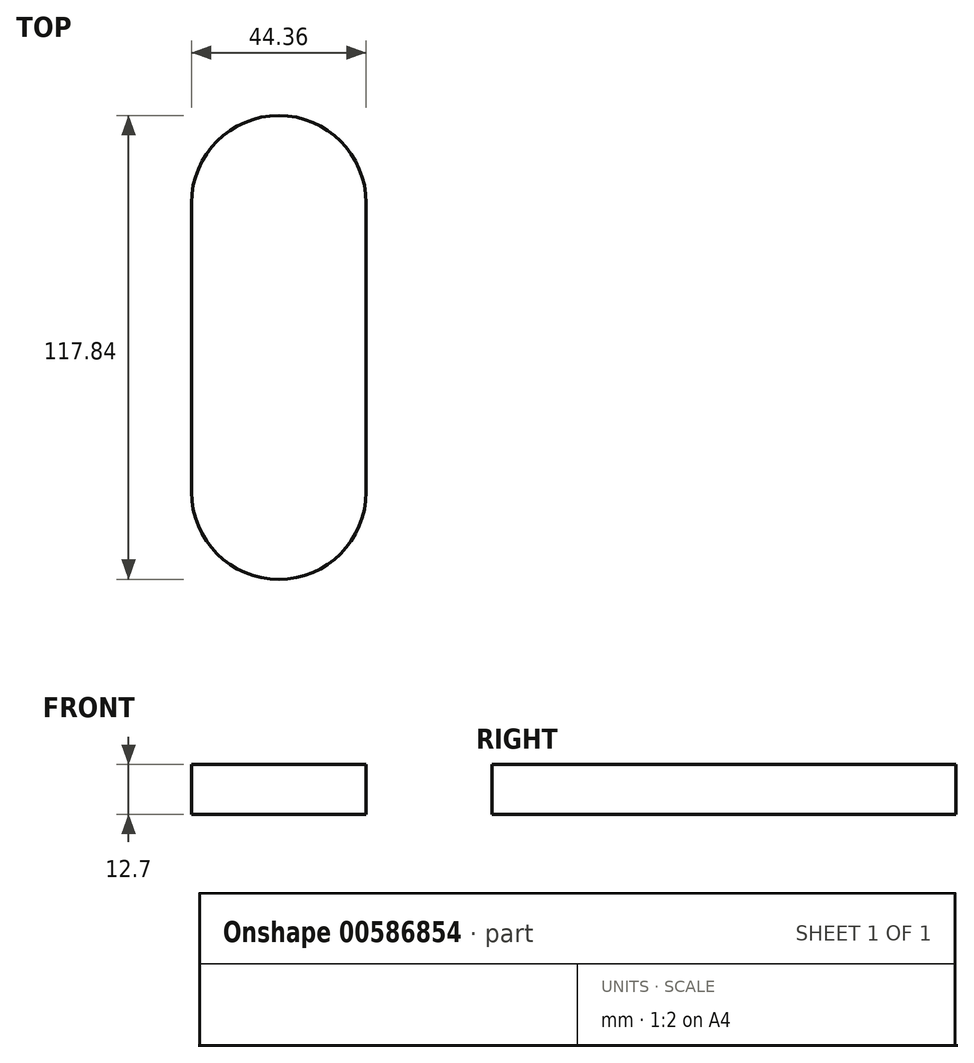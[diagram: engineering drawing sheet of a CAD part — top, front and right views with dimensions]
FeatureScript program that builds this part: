
annotation { "Feature Type Name" : "Feature", "Feature Type Description" : "" }
export const myFeature = defineFeature(function(context is Context, id is Id, definition is map)
    precondition{}
    {
        {
            var Q0;
            Q0=qCreatedBy(makeId("Top.planeOp"),FACE);
            var sketch = newSketch(context, id + "F0", { "sketchPlane" : qUnion([Q0])});
            skLineSegment(sketch, "E0.bottom", {"start": v(-21.1, 27.35) * mm, "end": v(23.27, 27.35) * mm});
            skLineSegment(sketch, "E0.top", {"start": v(-21.1, -46.13) * mm, "end": v(23.27, -46.13) * mm});
            skLineSegment(sketch, "E0.left", {"start": v(-21.1, 27.35) * mm, "end": v(-21.1, -46.13) * mm});
            skLineSegment(sketch, "E0.right", {"start": v(23.27, 27.35) * mm, "end": v(23.27, -46.13) * mm});
            skArc(sketch, "E1", {"start": v(23.27, 27.35) * mm, "mid": v(1.09, 49.53) * mm, "end": v(-21.1, 27.35) * mm});
            skArc(sketch, "E2", {"start": v(-21.1, -46.13) * mm, "mid": v(1.09, -68.3) * mm, "end": v(23.27, -46.13) * mm});
            skSolve(sketch);
        }
        {
            var Q0;
            Q0 = qSketchRegion(id + "F0", true);
            extrude(context, id + "F1", {"entities" : qUnion([Q0]), "depth" : 12.7 * mm, "offsetDistance" : 25.4 * mm});
        }
    });
